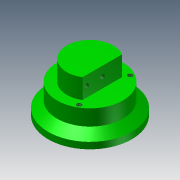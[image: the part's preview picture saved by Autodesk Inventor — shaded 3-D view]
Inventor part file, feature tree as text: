
AUTODESK INVENTOR PART (.ipt)
format: ipt  version: 2012 SP1 (Build 160190100, 190)  size: 203,776 bytes
history: native  units: in
note: dims shown in document units (in); Inventor stores cm internally (conversion verified against a paired STEP export)
features: sketch x5, hole x3, revolve x1, extrude x1, pattern_circular x1
ambient origin geometry x8: Origin, YZ Plane, XZ Plane, XY Plane, X Axis, Y Axis, Z Axis, Center Point
bodies: Solid1 (feature_tree)
feature tree (11):
  revolve  "Revolution1"  [1 undecoded]
  extrude  "Extrusion1"  Depth=0.9449in
  hole  "Hole1"  [1 undecoded]
  pattern_circular  "Circular Pattern1"  [2 undecoded]
  hole  "Hole2"  [1 undecoded]
  hole  "Hole3"  [1 undecoded]
  sketch  "Sketch1"  dims[d0=0.811in d1=1.15in]
  sketch  "Sketch2"  dims[d2=1.46in d3=0.9449in]
  sketch  "Sketch3"  dims[d4=0.3445in d6=0.113in]
  sketch  "Sketch5"  dims[d7=0.2756in]
  sketch  "Sketch7"  dims[d8=0.3543in d9=0.43in d11=0.811in d12=0.995in d13=0.1339in d14=0.2362in d15=90.0deg d16=0.689in d17=0.3937in d18=0.0in d19=0.5159in d20=1.15in d21=0.08in d22=0.2in d23=0.1575in d24=0.0787in d25=90.0deg d26=0.3in d27=0.8108in d28=1.1811in d29=360.0deg d43=0.06in d47=0.5941in d48=0.8268in d52=0.2756in d53=0.1722in d54=0.689in d55=0.3445in d56=0.3445in d57=0.276in d58=0.08in d59=0.1in d60=0.375in d61=0.25in d62=0.5635in d63=0.225in d64=0.8108in d65=0.09in d66=0.066in d67=0.055in d68=0.75in d69=0.375in d70=0.25in d71=0.5635in d72=0.8in d73=0.8108in]
note: 6 required parameter values undecoded (feature->parameter linkage not recoverable at this tier; creation-order binding heuristic only, values carry confidence <= 0.55)